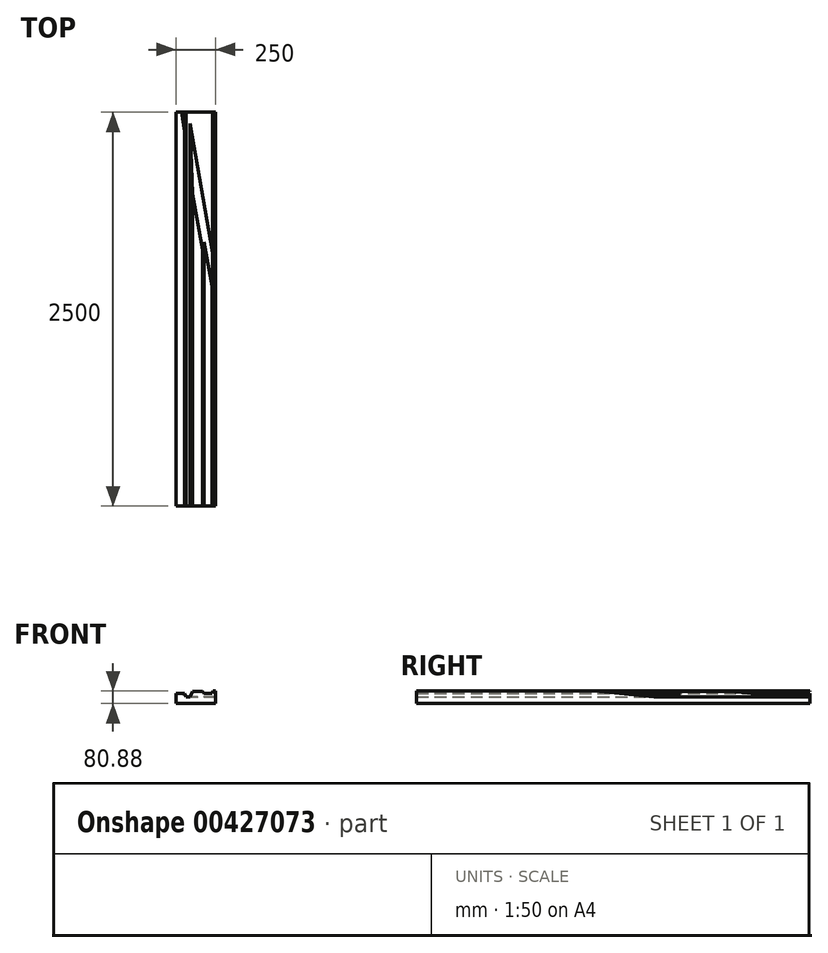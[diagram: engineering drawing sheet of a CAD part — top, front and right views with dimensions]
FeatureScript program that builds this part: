
annotation { "Feature Type Name" : "Feature", "Feature Type Description" : "" }
export const myFeature = defineFeature(function(context is Context, id is Id, definition is map)
    precondition{}
    {
        {
            var Q0;
            Q0=qCreatedBy(makeId("Front.planeOp"),FACE);
            var sketch = newSketch(context, id + "F0", { "sketchPlane" : qUnion([Q0])});
            skLineSegment(sketch, "E0.bottom", {"start": v(0, 0) * mm, "end": v(250, 0) * mm});
            skLineSegment(sketch, "E0.top", {"start": v(0, 88) * mm, "end": v(250, 88) * mm});
            skLineSegment(sketch, "E0.left", {"start": v(0, 0) * mm, "end": v(0, 88) * mm});
            skLineSegment(sketch, "E0.right", {"start": v(250, 0) * mm, "end": v(250, 88) * mm});
            skSolve(sketch);
        }
        {
            var Q0;
            Q0 = qSketchRegion(id + "F0", true);
            extrude(context, id + "F1", {"entities" : qUnion([Q0]), "depth" : 2500 * mm});
        }
        {
            var Q0;
            Q0=qCreatedBy(makeId("Front.planeOp"),FACE);
            var sketch = newSketch(context, id + "F2", { "sketchPlane" : qUnion([Q0])});
            skLineSegment(sketch, "E1", {"start": v(-6.03, 65.64) * mm, "end": v(54.95, 65.64) * mm});
            skLineSegment(sketch, "E2", {"start": v(54.95, 65.64) * mm, "end": v(63.96, 42.08) * mm});
            skLineSegment(sketch, "E3", {"start": v(63.96, 42.08) * mm, "end": v(87.52, 42.08) * mm});
            skLineSegment(sketch, "E4", {"start": v(87.52, 42.08) * mm, "end": v(105.54, 76.73) * mm});
            skLineSegment(sketch, "E5", {"start": v(105.54, 76.73) * mm, "end": v(167.9, 76.73) * mm});
            skLineSegment(sketch, "E6", {"start": v(167.9, 76.73) * mm, "end": v(179, 65.64) * mm});
            skLineSegment(sketch, "E7", {"start": v(179, 65.64) * mm, "end": v(228.2, 65.64) * mm});
            skLineSegment(sketch, "E8", {"start": v(228.2, 65.64) * mm, "end": v(233.74, 80.88) * mm});
            skLineSegment(sketch, "E9", {"start": v(233.74, 80.88) * mm, "end": v(266.3, 80.88) * mm});
            skLineSegment(sketch, "E10", {"start": v(266.3, 80.88) * mm, "end": v(266.3, 133.5) * mm});
            skLineSegment(sketch, "E11", {"start": v(266.3, 133.5) * mm, "end": v(-6.03, 133.5) * mm});
            skLineSegment(sketch, "E12", {"start": v(-6.03, 133.5) * mm, "end": v(-6.03, 65.64) * mm});
            skSolve(sketch);
        }
        {
            var Q0;
            Q0 = qSketchRegion(id + "F2", true);
            extrude(context, id + "F3", {"entities" : qUnion([Q0]), "operationType" : NewBodyOperationType.REMOVE, "endBound" : BoundingType.THROUGH_ALL, "depth" : 25 * mm});
        }
        {
            var Q0;
            Q0=makeQuery(id+"F3.boolean.opBoolean","COPY",FACE,{"derivedFrom":makeQuery(id+"F3.opExtrude","SWEPT_FACE",FACE,{"disambiguationData":[OSD([sQuery(id+"F2.wireOp",EDGE,"E3")])]})});
            var sketch = newSketch(context, id + "F4", { "sketchPlane" : qUnion([Q0])});
            skLineSegment(sketch, "E13", {"start": v(75, 0) * mm, "end": v(132.28, -324.86) * mm});
            skSolve(sketch);
        }
        {
            var Q0;
            Q0=sQuery(id+"F4.wireOp",EDGE,"E13");
            var Q1;
            Q1=sQuery(id+"F4.wireOp",VERTEX,"E13.start");
            cPlane(context, id + "F5", {"entities" : qUnion([Q0, Q1]), "cplaneType" : CPlaneType.CURVE_POINT, "offset" : 25 * mm, "width" : 150 * mm, "height" : 150 * mm});
        }
        {
            var Q0;
            Q0=qCreatedBy(id+"F5.planeOp",FACE);
            var sketch = newSketch(context, id + "F6", { "sketchPlane" : qUnion([Q0])});
            skLineSegment(sketch, "E14", {"start": v(73.86, 42.08) * mm, "end": v(13.85, 76.73) * mm});
            skLineSegment(sketch, "E15", {"start": v(13.85, 76.73) * mm, "end": v(295.86, 76.73) * mm});
            skLineSegment(sketch, "E16", {"start": v(295.86, 76.73) * mm, "end": v(295.86, 42.08) * mm});
            skLineSegment(sketch, "E17", {"start": v(295.86, 42.08) * mm, "end": v(73.86, 42.08) * mm});
            skSolve(sketch);
        }
        {
            var Q0;
            Q0 = qSketchRegion(id + "F6", true);
            extrude(context, id + "F7", {"entities" : qUnion([Q0]), "operationType" : NewBodyOperationType.REMOVE, "endBound" : BoundingType.THROUGH_ALL, "depth" : 25 * mm, "hasSecondDirection" : true, "secondDirectionOppositeDirection" : true, "secondDirectionDepth" : 25 * mm});
        }
    });
